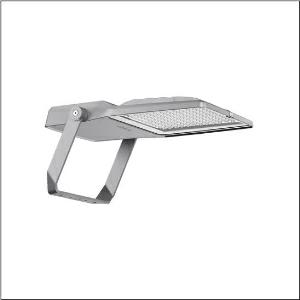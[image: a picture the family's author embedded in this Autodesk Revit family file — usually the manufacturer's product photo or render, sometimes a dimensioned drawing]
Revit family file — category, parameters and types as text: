
# Revit family: floodlight_fl_21_iq_midi___rs12_5xa7782e2b1a_51ba
name_source: partatom
category: Lighting Fixtures
units: mm (PartAtom-declared; Revit-internal decimal feet)

## family parameters
Cut with Voids When Loaded = No
Host = Face
Light Source = No
Part Type = Normal
Room Calculation Point = No
Round Connector Dimension = Use Diameter
Shared = No

## types (1)
- --- (1 x LED, 26730 lm, 208.1 W, 3000K)
    Apparent Load = 208 VA
    CIE Flux Codes = 79 92 99 100 100
    Color Rendering = 70
    Color Temperature = 3000K
    Default Elevation = 1800 mm
    Description = Floodlight FL 21 iQ midi, floodlight, primary light control with lens, of PMMA, primary optical cover: protective disc, of toughened safety glass, transparent, light distribution: RS12, light emission: direct distribution, installation type: surface-mounted, LED, High Power LED, rated luminous flux: 26.730lm, luminous efficacy: 128lm/W, light colour: 730, colour temperature: 3000K, control gear: ECG iQ, control: optimised constant luminous flux control (CLO 2.0), Desk-Remote (wireless, voltage-free reading and setting of iQ features in the workshop via application-optimized NFC function/RFID function), Smart-Wire, Night-Set, Temp-Guard, Street-Remote, Auto-Match, with terminal, 6-pole, mains connection: 220..240V, AC, 50/60Hz, start of lifetime: 208W, end of service life: 227W, reduction: 90W, luminaire housing, of diecast aluminium, powder-coated, Siteco® metallic grey (DB 702S), corrosivity category C5 mid according to DIN EN ISO 12944, sealing non-destructively replaceable, mounting bracket, of steel, galvanised, powder-coated, Siteco® metallic grey (DB 702S), protection rating (complete): IP66, insulation class (complete): insulation class II (safety insulation), certification: CE, protection symbol: D, impact resistance: IK08, permissible operating ambient temperature: -40..+40°C, permissible operating ambient temperature for outdoor applications: -40..+50°C, standard: DIN EN 12944, LABS conformity tested according to VDMA 24364:2018-05, packaging unit: 1 piece

Light Distribution: RS12
    Height = 76 mm
    Lamp = 1 x LED
    Lamp Light Flux = 26730 lm
    Lamp Power = 208.1 W
    Lamp count = 1
    Length = 657 mm
    Luminous efficacy = 128 lm/W
    Manufacturer = Siteco
    ModVariant = No
    Model = 5XA7782E2B1A
    Number of Poles = 1
    OnlyDefault = Yes
    Power Factor = 1
    Product Name = Floodlight FL 21 iQ midi | RS12
    Product group = floodlight | pylon annexe
    ProductGroupID = 6200
    Protection Class = Protection class II
    Protection Degree = IP 66
    RLX_Detail_Level = 1
    RLX_Emergency_Light_Flux = 0 lm
    RLX_Emergency_Type = 0
    RLX_Emergency_Type_DB = No
    RlxData = <blob elided: 141085 chars, md5=7f285adb>
    Socket = socket
    Standby Power = 0 W
    System Light Flux = 26730 lm
    System Power = 208 W
    Type Comments = factory setting: luminous flux: 100 % | dim-lin: 254 | 710 mA
    Type Image = l_1006876.jpg
    URL = http://relux.com
    VarID = @adj_056103
    Voltage = 0 V
    Weight = 0.00 kg
    Width = 442 mm

## geometry (parser evidence)
native form markers: Blend x4, Sweep x12
no freeform markers — native parametric forms only
